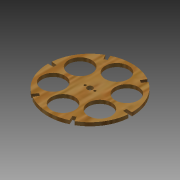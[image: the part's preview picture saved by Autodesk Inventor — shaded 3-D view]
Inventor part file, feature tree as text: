
AUTODESK INVENTOR PART (.ipt)
format: ipt  version: 2013 (Build 170138000, 138)  size: 158,720 bytes
history: native  units: in
note: dims shown in document units (in); Inventor stores cm internally (conversion verified against a paired STEP export)
features: sketch x3, extrude x2, hole x1, pattern_circular x1
ambient origin geometry x8: Origin, YZ Plane, XZ Plane, XY Plane, X Axis, Y Axis, Z Axis, Center Point
bodies: Solid1 (feature_tree)
feature tree (7):
  extrude  "Extrusion1"  Depth=1.9232in
  hole  "Hole1"  [1 undecoded]
  extrude  "Extrusion2"  Depth=0.25in TaperAngle=0.0deg
  pattern_circular  "Circular Pattern1"  [2 undecoded]
  sketch  "Sketch1"  dims[d0=1.6535in d2=1.9232in]
  sketch  "Sketch2"  dims[d3=2.3622in d5=360.0deg d7=6.0in]
  sketch  "Sketch3"  dims[d8=0.4in d9=0.25in d10=0.0in d11=0.7in d13=0.1695in d14=0.75in d15=0.375in d16=0.25in d17=0.5635in d18=1.0in d19=0.8108in d24=0.0in d25=0.0in d26=2.3622in d27=360.0deg d30=60.0deg d35=0.7874in d37=0.7874in d38=0.4466in]
note: 3 required parameter values undecoded (feature->parameter linkage not recoverable at this tier; creation-order binding heuristic only, values carry confidence <= 0.55)
